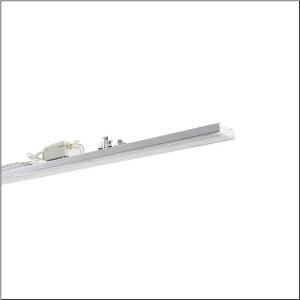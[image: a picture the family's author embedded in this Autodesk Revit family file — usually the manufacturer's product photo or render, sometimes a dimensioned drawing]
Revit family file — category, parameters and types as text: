
# Revit family: licross_21_recessed_ho_51te11vn4c5sd
name_source: partatom
category: Lighting Fixtures
units: mm (PartAtom-declared; Revit-internal decimal feet)

## family parameters
Cut with Voids When Loaded = No
Host = Face
Light Source = No
Part Type = Normal
Room Calculation Point = No
Round Connector Dimension = Use Diameter
Shared = No

## types (1)
- --- (1 x LED, 2050 lm, 12.3 W, 4000K)
    Apparent Load = 12 VA
    CIE Flux Codes = 84 94 98 99 100
    Color Rendering = 80
    Color Temperature = 4000K
    Default Elevation = 1800 mm
    Description = Licross 21 Recessed HO, luminaire insert, of sheet steel, galvanised, coil coated, white, length: 1.500mm, width: 66mm, height: 67mm, LED rated luminous flux: 12.960lm, light colour: 840, SDCM (Standard Deviation of Colour Matching)MacAdam ≤ 2 SDCM (initial), control gear: DALI 2, CLO (for two DALI lines), with plug, 6-pole, with phase selection, mains connection: 220..240V, AC/DC, 0/50..60Hz, start of lifetime: 71W, end of service life: 77W, internal wiring halogen-free, for central battery installations according to EN 60598-2-22, for emergency light function, without changeover relay, primary optical cover: cover, of PMMA, light emission: direct distribution, primary light characteristic: symmetric, protection rating (complete): IP54, insulation class (complete): insulation class I (protective earthing), certification: CE, ENEC, VDE, UKCA, protection symbol: D if used in an environment with non-conductive dust loads with corresponding accessories, impact resistance: IK06, permissible ambient temperature for indoor applications: -25..+35°C, standard: EN 60598-2-22, corresponds to IFS (International Featured Standards) requirements for safety and quality in the food industry, reducing of maximum allowable ambient temperature of 5°C with ceiling mounting, LABS conformity tested according to VDMA 24364:2018-05, The light source and the operating device comply with the requirements of the Ecodesign Regulation (EU) 2019/2020 and are replaceable in accordance with this regulation, packaging unit: 1 piece
    Height = 58 mm
    Lamp = 1 x LED
    Lamp Light Flux = 2050 lm
    Lamp Power = 12.3 W
    Lamp count = 1
    Length = 1500 mm
    Luminous efficacy = 167 lm/W
    Manufacturer = Siteco
    ModVariant = No
    Model = 51TE11VN4C5SD
    Mounting Place = Ceiling
    Mounting Type = Pendant
    Number of Poles = 1
    OnlyDefault = Yes
    Power Factor = 1
    Product Name = Licross 21 Recessed HO
    Product group = luminaire insert | ceiling pendant
    ProductGroupID = 901
    Protection Class = Protection class I
    Protection Degree = IP 54
    RLX_Detail_Level = 1
    RLX_Emergency_Light_Flux = 0 lm
    RLX_Emergency_Type = 0
    RLX_Emergency_Type_DB = No
    RlxData = <blob elided: 25621 chars, md5=5d0afc4f>
    Socket = socket
    Standby Power = 0 W
    System Light Flux = 2050 lm
    System Power = 12 W
    Type Comments = : DC mode (central or group accumulator) initial emergency light level
    Type Image = l_1296930.jpg
    URL = http://relux.com
    VarID = @adj_000729
    Voltage = 0 V
    Weight = 0.00 kg
    Width = 66 mm

## geometry (parser evidence)
native form markers: Blend x4, Sweep x10
no freeform markers — native parametric forms only
